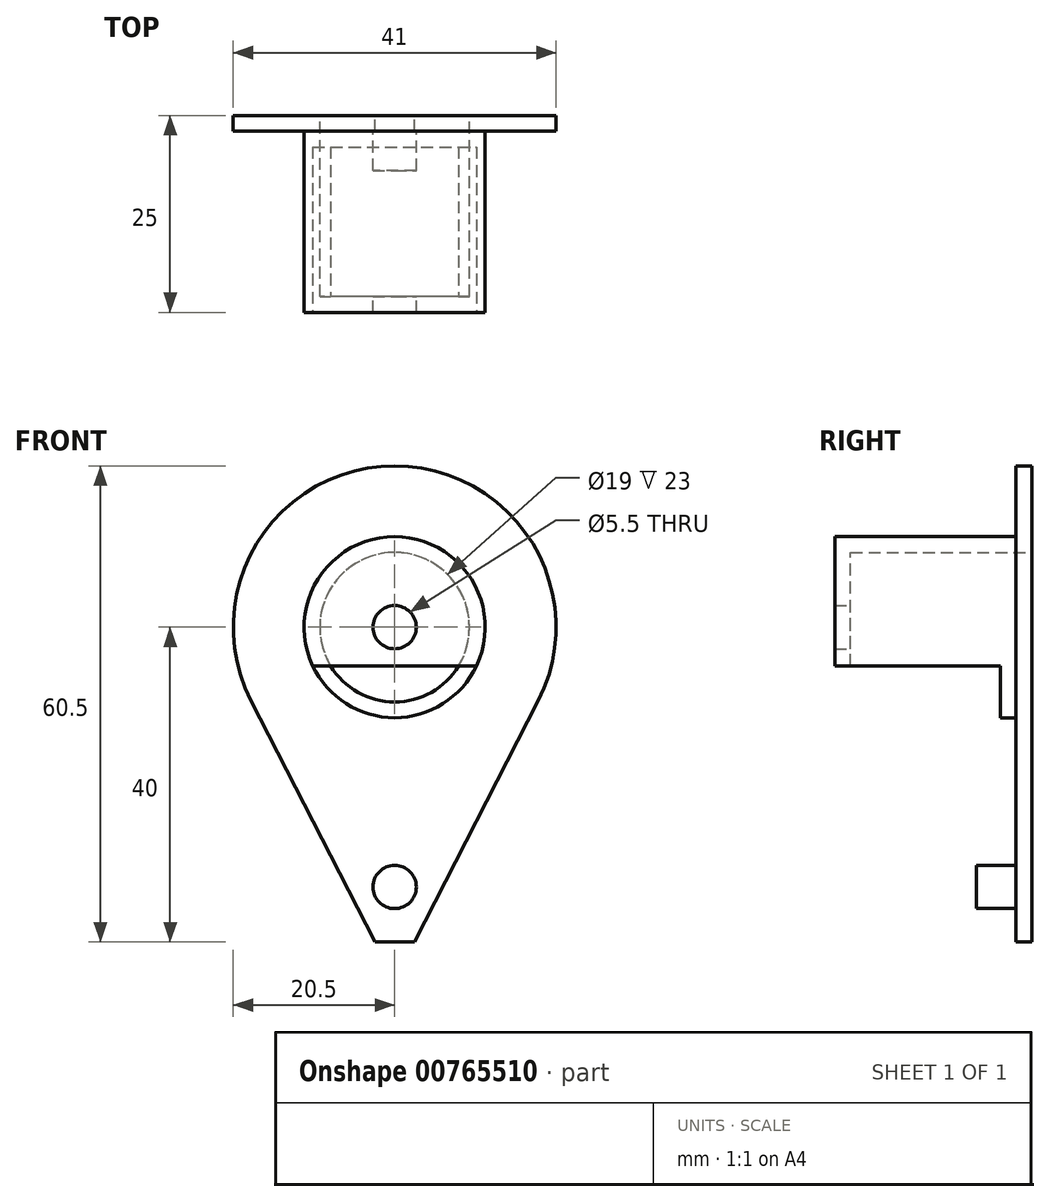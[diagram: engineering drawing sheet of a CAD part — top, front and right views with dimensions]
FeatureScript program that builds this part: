
annotation { "Feature Type Name" : "Feature", "Feature Type Description" : "" }
export const myFeature = defineFeature(function(context is Context, id is Id, definition is map)
    precondition{}
    {
        {
            var Q0;
            Q0=qCreatedBy(makeId("Front.planeOp"),FACE);
            var sketch = newSketch(context, id + "F0", { "sketchPlane" : qUnion([Q0])});
            skCircle(sketch, "E0", {"center": v(0, 0) * mm, "radius": 11.5 * mm});
            skArc(sketch, "E1", {"start": v(18.24, -9.37) * mm, "mid": v(0, 20.5) * mm, "end": v(-18.24, -9.37) * mm});
            skLineSegment(sketch, "E2", {"start": v(-2.5, -40) * mm, "end": v(2.5, -40) * mm});
            skLineSegment(sketch, "E3", {"start": v(-2.5, -40) * mm, "end": v(-18.24, -9.37) * mm});
            skLineSegment(sketch, "E4", {"start": v(2.5, -40) * mm, "end": v(18.24, -9.37) * mm});
            skCircle(sketch, "E5", {"center": v(0, 0) * mm, "radius": 9.5 * mm});
            skCircle(sketch, "E6", {"center": v(0, -33) * mm, "radius": 2.75 * mm});
            skSolve(sketch);
        }
        {
            var Q0;
            Q0=makeQuery(id+"F0.imprint","IMPRINT",FACE,{"disambiguationData":[TD([[makeQuery(id+"F0.imprint","IMPRINT",EDGE,{"derivedFrom":sQuery(id+"F0.wireOp",EDGE,"E0")}),-1.0]])]});
            extrude(context, id + "F1", {"entities" : qUnion([Q0]), "depth" : 2 * mm, "offsetDistance" : 25 * mm});
        }
        {
            var Q0;
            Q0=makeQuery(id+"F1.opExtrude","CAP_FACE",FACE,{"disambiguationData":[OSD([sQuery(id+"F0.wireOp",EDGE,"E0"),sQuery(id+"F0.wireOp",EDGE,"E1"),sQuery(id+"F0.wireOp",EDGE,"E2"),sQuery(id+"F0.wireOp",EDGE,"E3"),sQuery(id+"F0.wireOp",EDGE,"E4")])],"isStart":true});
            var sketch = newSketch(context, id + "F2", { "sketchPlane" : qUnion([Q0])});
            skArc(sketch, "E7", {"start": v(-11.5, 0) * mm, "mid": v(8.13, -8.13) * mm, "end": v(0, 11.5) * mm});
            skLineSegment(sketch, "E8", {"start": v(10.36, -5) * mm, "end": v(-10.36, -5) * mm});
            skArc(sketch, "E9", {"start": v(8.66, -5) * mm, "mid": v(0, 10) * mm, "end": v(-8.66, -5) * mm});
            skSolve(sketch);
        }
        {
            var Q0;
            {var subQ3=sQuery(id+"F2.wireOp",EDGE,"E8");Q0=makeQuery(id+"F2.imprint","IMPRINT",FACE,{"disambiguationData":[TD([[makeQuery(id+"F2.imprint","IMPRINT",EDGE,{"derivedFrom":subQ3}),-1.0]])]});}
            extrude(context, id + "F3", {"entities" : qUnion([Q0]), "depth" : 29 * mm, "offsetDistance" : 25 * mm});
        }
        {
            var Q0;
            Q0=qCreatedBy(makeId("Front.planeOp"),FACE);
            var sketch = newSketch(context, id + "F4", { "sketchPlane" : qUnion([Q0])});
            skCircle(sketch, "E10", {"center": v(0, 0) * mm, "radius": 11.5 * mm});
            skCircle(sketch, "E11", {"center": v(0, 0) * mm, "radius": 2.75 * mm});
            skSolve(sketch);
        }
        {
            var Q0;
            Q0=makeQuery(id+"F4.imprint","IMPRINT",FACE,{"disambiguationData":[TD([[makeQuery(id+"F4.imprint","IMPRINT",EDGE,{"derivedFrom":sQuery(id+"F4.wireOp",EDGE,"E10")}),1.0]])]});
            extrude(context, id + "F5", {"entities" : qUnion([Q0]), "depth" : 2 * mm, "offsetDistance" : 25 * mm});
        }
        {
            var Q0;
            Q0=makeQuery(id+"F5.opExtrude","SWEPT_BODY",BODY,{"disambiguationData":[OSD([sQuery(id+"F4.wireOp",EDGE,"E10"),sQuery(id+"F4.wireOp",EDGE,"E11")])]});
            deleteBodies(context, id + "F6", {"entities" : qUnion([Q0])});
        }
        {
            var Q0;
            Q0=makeQuery(id+"F3.opExtrude","SWEPT_BODY",BODY,{"disambiguationData":[OSD([sQuery(id+"F0.wireOp",EDGE,"E0"),sQuery(id+"F2.wireOp",EDGE,"E7"),sQuery(id+"F2.wireOp",EDGE,"E8"),sQuery(id+"F2.wireOp",EDGE,"E9")])]});
            deleteBodies(context, id + "F7", {"entities" : qUnion([Q0])});
        }
        {
            var Q0;
            Q0=makeQuery(id+"F0.imprint","IMPRINT",FACE,{"disambiguationData":[TD([[makeQuery(id+"F0.imprint","IMPRINT",EDGE,{"derivedFrom":sQuery(id+"F0.wireOp",EDGE,"E0")}),1.0]])]});
            extrude(context, id + "F8", {"entities" : qUnion([Q0]), "operationType" : NewBodyOperationType.ADD, "depth" : 23 * mm, "offsetDistance" : 25 * mm});
        }
        {
            var Q0;
            Q0=makeQuery(id+"F0.imprint","IMPRINT",FACE,{"disambiguationData":[TD([[makeQuery(id+"F0.imprint","IMPRINT",EDGE,{"derivedFrom":sQuery(id+"F0.wireOp",EDGE,"E6")}),1.0]])]});
            extrude(context, id + "F9", {"entities" : qUnion([Q0]), "operationType" : NewBodyOperationType.ADD, "depth" : 7 * mm, "offsetDistance" : 25 * mm});
        }
        {
            var Q0;
            Q0=makeQuery(id+"F8.opExtrude","CAP_FACE",FACE,{"disambiguationData":[OSD([sQuery(id+"F0.wireOp",EDGE,"E0"),sQuery(id+"F0.wireOp",EDGE,"E5")])],"isStart":false});
            var sketch = newSketch(context, id + "F10", { "sketchPlane" : qUnion([Q0])});
            skLineSegment(sketch, "E12", {"start": v(-10.4, -4.92) * mm, "end": v(10.4, -4.92) * mm});
            skSolve(sketch);
        }
        {
            var Q0;
            Q0 = qSketchRegion(id + "F10", true);
            var Q1;
            {var subQ0=sQuery(id+"F10.wireOp",EDGE,"E12");var subQ1=makeQuery(id+"F8.opExtrude","CAP_EDGE",EDGE,{"disambiguationData":[OSD([sQuery(id+"F0.wireOp",EDGE,"E0")])],"isStart":false});var subQ2=makeQuery(id+"F10.imprint","INTERSECT",VERTEX,{"disambiguationData":[OD(0.0)],"derivedFrom":[subQ1,subQ0]});Q1=makeQuery(id+"F10.imprint","IMPRINT",FACE,{"disambiguationData":[TD([[makeQuery(id+"F10.imprint","IMPRINT",EDGE,{"disambiguationData":[TD([[subQ2,-1.0]])],"derivedFrom":subQ0}),-1.0]])]});}
            extrude(context, id + "F11", {"entities" : qUnion([Q0, Q1]), "operationType" : NewBodyOperationType.REMOVE, "oppositeDirection" : true, "depth" : 19 * mm, "offsetDistance" : 25 * mm});
        }
        {
            var Q0;
            Q0=makeQuery(id+"F8.opExtrude","CAP_FACE",FACE,{"disambiguationData":[OSD([sQuery(id+"F0.wireOp",EDGE,"E0"),sQuery(id+"F0.wireOp",EDGE,"E5")])],"isStart":false});
            var sketch = newSketch(context, id + "F12", { "sketchPlane" : qUnion([Q0])});
            skLineSegment(sketch, "E13", {"start": v(10.4, -4.92) * mm, "end": v(-10.4, -4.92) * mm});
            skCircle(sketch, "E14", {"center": v(0, 0) * mm, "radius": 2.75 * mm});
            skSolve(sketch);
        }
        {
            var Q0;
            {var subQ1=makeQuery(id+"F8.opExtrude","CAP_EDGE",EDGE,{"disambiguationData":[OSD([sQuery(id+"F0.wireOp",EDGE,"E5")])],"isStart":false});Q0=makeQuery(id+"F12.imprint","IMPRINT",FACE,{"disambiguationData":[TD([[makeQuery(id+"F12.imprint","IMPRINT",EDGE,{"derivedFrom":subQ1}),1.0]])]});}
            var Q1;
            {var subQ1=makeQuery(id+"F8.opExtrude","CAP_EDGE",EDGE,{"disambiguationData":[OSD([sQuery(id+"F0.wireOp",EDGE,"E0")])],"isStart":false});Q1=makeQuery(id+"F12.imprint","IMPRINT",FACE,{"disambiguationData":[TD([[makeQuery(id+"F12.imprint","IMPRINT",EDGE,{"derivedFrom":subQ1}),1.0]])]});}
            extrude(context, id + "F13", {"entities" : qUnion([Q0, Q1]), "operationType" : NewBodyOperationType.ADD, "depth" : 2 * mm, "offsetDistance" : 25 * mm});
        }
    });
